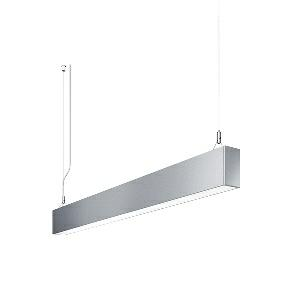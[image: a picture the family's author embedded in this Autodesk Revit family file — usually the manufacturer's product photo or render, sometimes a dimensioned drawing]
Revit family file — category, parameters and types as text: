
# Revit family: dotoo_line_-_dlp_2000_840_d_00805825_8819
name_source: partatom
category: Lighting Fixtures
units: mm (PartAtom-declared; Revit-internal decimal feet)

## family parameters
Cut with Voids When Loaded = No
Host = Face
Light Source = No
Part Type = Normal
Room Calculation Point = No
Round Connector Dimension = Use Diameter
Shared = No

## types (1)
- DOTOO.line - DLP 2000/840/D (1 x LED, 1700 lm, 4000K)
    Apparent Load = 16 VA
    Approval mark = CE
    CIE Flux Codes = 67 91 98 100 100
    Color Rendering = 80-89
    Color Temperature = 4000K
    Control Gear = Electronic ballast
    Default Elevation = 1800 mm
    Description = DLP 2000/840/D|Suspended luminaire|light source: LED|connected load: 220-240 V, 50/60 Hz|Power consumption: approx. 16 W|standby: approx. 0,15|luminous flux: 1700 lm|luminous efficacy: 106 lm/W|light distribution: Direct|direct ratio: approx. 100 %|colour temperature: Cold white, ca. 4000 K|color rendering index (CRI): >= 80|chromaticity tolerance:  3 SDCM|System of protection: IP 40|technology: Continuously dimmable|luminaire body|material: Sectional aluminium|colour: Silver|lamp cover: Acrylic (PMMA), Clear|mains lead: 2.00 m With free stranded wires|Fastening: Steel cable 0.3 - 0.7 m|glare control: Prism aperture|luminance(L65): <= 3000 cd/m|unified glare rating(4H 8H): <=  19|special features: DALI Load 1x, TouchDIM - dimming via standard switch, Flicker-free, Suitable as emergency lighting|
    Frequency = 50 Hz
    Height = 110 mm
    Lamp = 1 x LED
    Lamp Light Flux = 1700 lm
    Lamp count = 1
    Length = 1414 mm
    Luminous efficacy = 106 lm/W
    Manufacturer = Waldmann
    ModVariant = No
    Model = 00805825
    Mounting Place = Ceiling
    Mounting Type = Pendant
    Number of Poles = 1
    OnlyDefault = Yes
    Power Factor = 1
    Product Name = DOTOO.line - DLP 2000/840/D
    Product group = Suspended luminaire
    ProductGroupID = 9
    Protection Class = Protection class I
    Protection Degree = IP 40
    RLX_Detail_Level = 1
    RLX_Emergency_Light_Flux = 0 lm
    RLX_Emergency_Type = 0
    RLX_Emergency_Type_DB = No
    RlxData = <blob elided: 21749 chars, md5=14729d07>
    Socket = socket
    Standby Power = 0 W
    System Light Flux = 1700 lm
    System Power = 16 W
    Type Comments = Product without accessories
    Type Image = 113292000-00692525.jpg
    URL = http://relux.com
    VarID = ---
    Voltage = 230 V
    Voltage Range = 220-240 V
    Weight = 0.00 kg
    Width = 60 mm  [stored 0.19685 ft]

note: [stored X ft] marks values corroborated as IEEE doubles in the binary element streams (Revit-internal decimal feet)

## geometry (parser evidence)
native form markers: Blend x4, Sweep x12
no freeform markers — native parametric forms only
